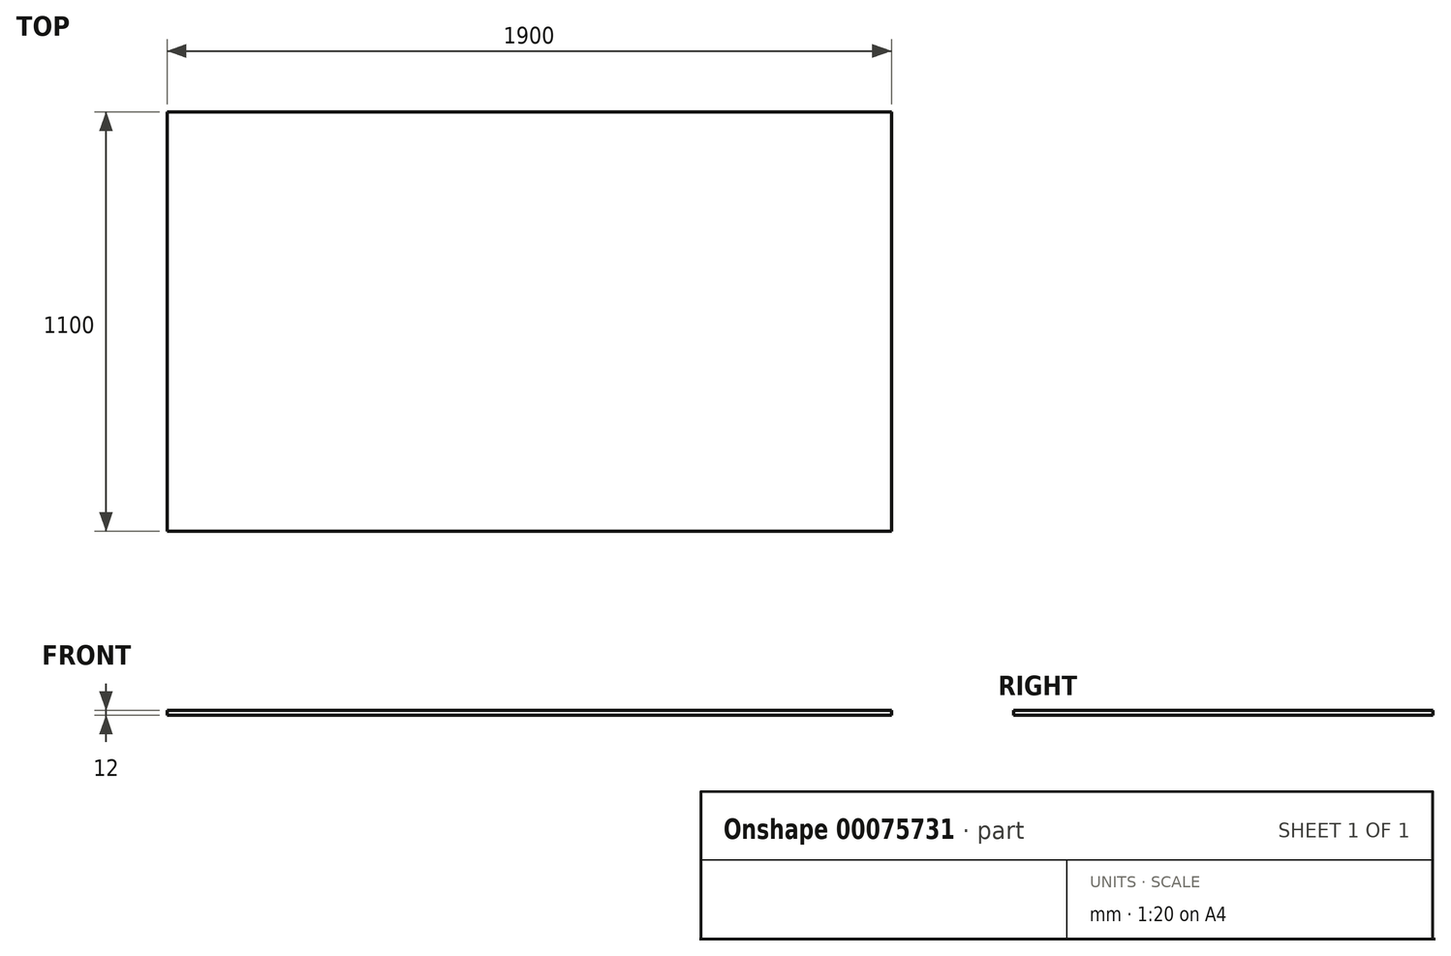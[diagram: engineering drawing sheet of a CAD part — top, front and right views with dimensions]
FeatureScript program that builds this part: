
annotation { "Feature Type Name" : "Feature", "Feature Type Description" : "" }
export const myFeature = defineFeature(function(context is Context, id is Id, definition is map)
    precondition{}
    {
        {
            var Q0;
            Q0=qCreatedBy(makeId("Top.planeOp"),FACE);
            var sketch = newSketch(context, id + "F0", { "sketchPlane" : qUnion([Q0])});
            skLineSegment(sketch, "E0.bottom", {"start": v(-874.89, -605.9) * mm, "end": v(1025.11, -605.9) * mm});
            skLineSegment(sketch, "E0.top", {"start": v(-874.89, 494.1) * mm, "end": v(1025.11, 494.1) * mm});
            skLineSegment(sketch, "E0.left", {"start": v(-874.89, -605.9) * mm, "end": v(-874.89, 494.1) * mm});
            skLineSegment(sketch, "E0.right", {"start": v(1025.11, -605.9) * mm, "end": v(1025.11, 494.1) * mm});
            skSolve(sketch);
        }
        {
            var Q0;
            Q0=makeQuery(id+"F0.imprint","IMPRINT",FACE,{"disambiguationData":[TD([[makeQuery(id+"F0.imprint","IMPRINT",EDGE,{"derivedFrom":sQuery(id+"F0.wireOp",EDGE,"E0.bottom")}),1.0]])]});
            extrude(context, id + "F1", {"entities" : qUnion([Q0]), "depth" : 12 * mm});
        }
    });
